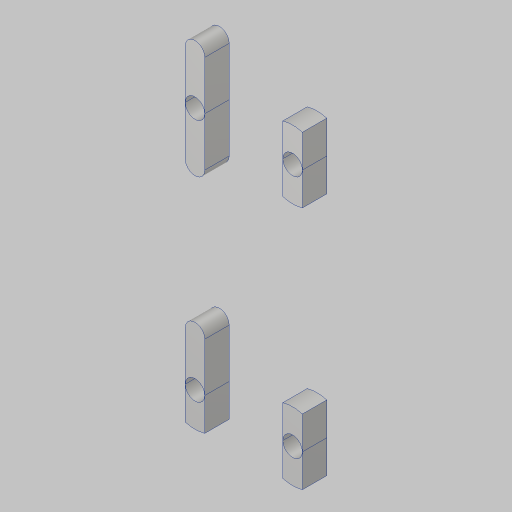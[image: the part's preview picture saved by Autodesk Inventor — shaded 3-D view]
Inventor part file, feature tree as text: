
AUTODESK INVENTOR PART (.ipt)
format: ipt  version: 2023.5 (Build 275446000, 446)  size: 335,360 bytes
history: native  units: in
note: dims shown in document units (in); Inventor stores cm internally (conversion verified against a paired STEP export)
features: sketch x4, hole x3, extrude x2, fillet x2, projected_geometry x2
ambient origin geometry x8: Origin, YZ Plane, XZ Plane, XY Plane, X Axis, Y Axis, Z Axis, Center Point
bodies: Solid1 (feature_tree)
feature tree (13):
  sketch  "Sketch1"  dims[d0=2.0in d1=15.0in]
  sketch  "Sketch2"  dims[d2=0.875in d3=17.0in d4=2.0in]
  extrude  "Extrusion1"  Depth=15.0in
  hole  "Hole1"  [1 undecoded]
  fillet  "Fillet1"  Radius=2.0in
  hole  "Hole2"  [1 undecoded]
  hole  "Hole3"  [1 undecoded]
  extrude  "Extrusion2"  Depth=1.0in
  fillet  "Fillet2"  Radius=3.6in
  sketch  "Sketch3"  dims[d5=17.0in d6=1.0in]
  projected_geometry  "Projected Loop1"
  sketch  "Sketch4"  dims[d7=0.2405in d8=2.4in d9=0.5in d10=3.6in d11=1.5in d12=1.5in d13=0.9in d14=3.7in d15=1.0in d16=3.4in d22=1.125in d23=4.297in d24=0.25in d25=2.0in d26=2.3622in d28=360.0deg d30=7.0in d31=2.0in d32=0.201in d33=1.0in d34=1.5in d35=1.0in d36=0.201in d37=1.0in d38=1.0in d39=2.5in d40=0.25in d41=0.0in d42=0.85in d43=0.201in d44=0.75in d45=0.385in d46=0.25in d47=0.5635in d48=1.0in d49=0.8108in d50=0.375in d51=0.26in d53=0.156in d54=0.38in d55=0.385in d56=0.25in d57=0.5635in d58=1.0in d59=0.8108in d65=0.25in d66=0.125in d67=0.125in d68=0.125in d69=0.125in d70=2.5in d71=0.125in d72=0.125in d73=0.125in d74=0.125in d75=1.0in d76=0.0in d77=0.0in d78=0.13in d83=0.156in d84=0.38in d85=0.375in d86=0.25in d87=0.5635in d88=1.0in d89=0.8108in d90=0.125in d91=0.125in]
  projected_geometry  "Projected Loop2"
note: 3 required parameter values undecoded (feature->parameter linkage not recoverable at this tier; creation-order binding heuristic only, values carry confidence <= 0.55)
